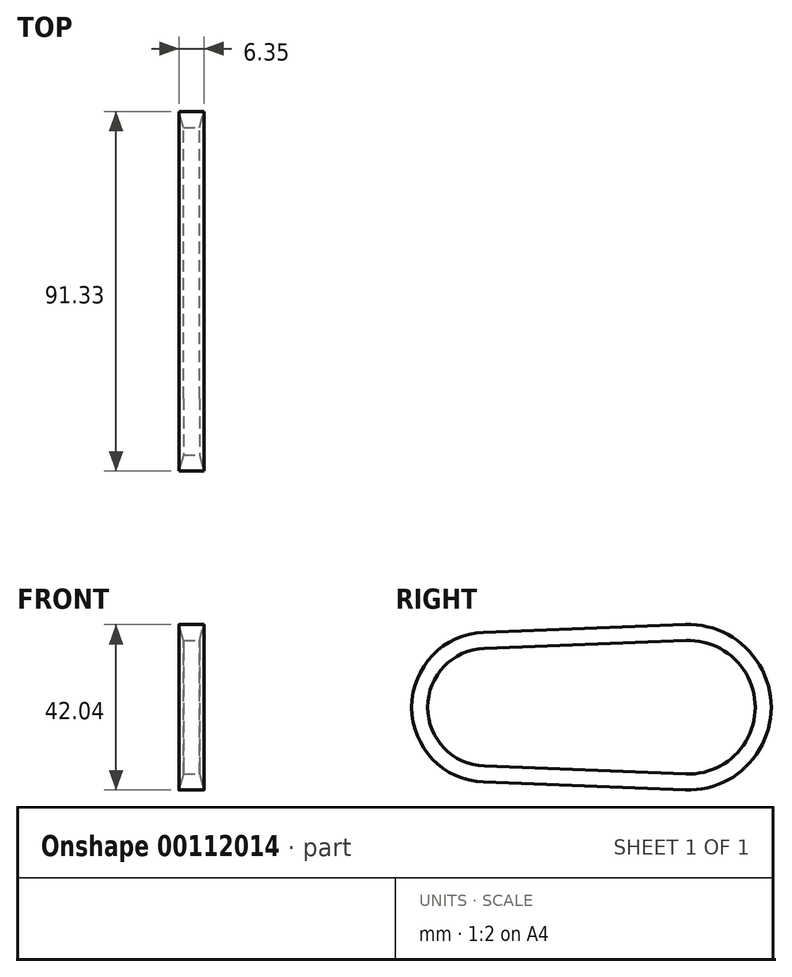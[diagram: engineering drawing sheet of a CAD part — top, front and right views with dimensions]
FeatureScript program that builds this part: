
annotation { "Feature Type Name" : "Feature", "Feature Type Description" : "" }
export const myFeature = defineFeature(function(context is Context, id is Id, definition is map)
    precondition{}
    {
        {
            var Q0;
            Q0=qCreatedBy(makeId("Right.planeOp"),FACE);
            var sketch = newSketch(context, id + "F0", { "sketchPlane" : qUnion([Q0])});
            skArc(sketch, "E0", {"start": v(-0.82, -21.02) * mm, "mid": v(21.04, 0) * mm, "end": v(-0.82, 21.02) * mm});
            skArc(sketch, "E1", {"start": v(-52.02, 19.04) * mm, "mid": v(-70.33, 0) * mm, "end": v(-52.02, -19.04) * mm});
            skLineSegment(sketch, "E2", {"start": v(-52.02, 19.04) * mm, "end": v(-0.82, 21.02) * mm});
            skLineSegment(sketch, "E3", {"start": v(-0.82, -21.02) * mm, "end": v(-52.02, -19.04) * mm});
            skSolve(sketch);
        }
        {
            var Q0;
            Q0=qCreatedBy(makeId("Front.planeOp"),FACE);
            var sketch = newSketch(context, id + "F1", { "sketchPlane" : qUnion([Q0])});
            skLineSegment(sketch, "E4", {"start": v(0, 21.02) * mm, "end": v(6.35, 21.02) * mm});
            skLineSegment(sketch, "E5", {"start": v(6.35, 21.02) * mm, "end": v(5.26, 16.96) * mm});
            skLineSegment(sketch, "E6", {"start": v(5.26, 16.96) * mm, "end": v(1.09, 16.96) * mm});
            skLineSegment(sketch, "E7", {"start": v(1.09, 16.96) * mm, "end": v(0, 21.02) * mm});
            skSolve(sketch);
        }
        {
            var Q0;
            Q0=makeQuery(id+"F1.imprint","IMPRINT",FACE,{"disambiguationData":[TD([[makeQuery(id+"F1.imprint","IMPRINT",EDGE,{"derivedFrom":sQuery(id+"F1.wireOp",EDGE,"E4")}),-1.0]])]});
            var Q1;
            Q1=sQuery(id+"F0.wireOp",EDGE,"E2");
            var Q2;
            Q2=sQuery(id+"F0.wireOp",EDGE,"E1");
            var Q3;
            Q3=sQuery(id+"F0.wireOp",EDGE,"E3");
            var Q4;
            Q4=sQuery(id+"F0.wireOp",EDGE,"E0");
            sweep(context, id + "F2", {"profiles" : qUnion([Q0]), "path" : qUnion([Q1, Q2, Q3, Q4])});
        }
    });
